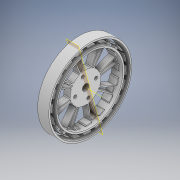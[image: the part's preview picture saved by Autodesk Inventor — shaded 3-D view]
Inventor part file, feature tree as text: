
AUTODESK INVENTOR PART (.ipt)
format: ipt  version: 2020 (Build 240168000, 168)  size: 643,072 bytes
history: native  units: mm
features: sketch x9, extrude x7, chamfer x2, pattern_circular x2, revolve x2, plane x1, fillet x1, other x1
ambient origin geometry x8: Origin, YZ Plane, XZ Plane, XY Plane, X Axis, Y Axis, Z Axis, Center Point
bodies: Solid1 (feature_tree)
feature tree (25):
  extrude  "Extrusion1"  Depth=7.0mm TaperAngle=0.0deg
  extrude  "Extrusion3"  Depth=80.0mm TaperAngle=360.0deg
  extrude  "Extrusion4"  Depth=7.0mm
  extrude  "Extrusion5"  Depth=13.6mm
  plane  "Work Plane2"
  sketch  "Sketch8"  dims[d25=4.0mm d26=2.0mm]
  extrude  "Extrusion7"  Depth=2.0mm
  extrude  "Extrusion8"  Depth=7.0mm TaperAngle=0.0deg
  chamfer  "Chamfer1"  Distance=7.0mm
  pattern_circular  "Circular Pattern1"  [2 undecoded]
  chamfer  "Chamfer2"  Distance=5.0mm
  fillet  "Fillet1"  Radius=0.5mm
  sketch  "Sketch10"  dims[d33=43.0mm]
  other  "Work Axis1"
  sketch  "Sketch11"  dims[d34=47.0mm]
  revolve  "Revolution2"  Angle=360.0deg
  revolve  "Revolution3"  Angle=45.0deg
  pattern_circular  "Circular Pattern2"  [2 undecoded]
  extrude  "Extrusion9"  Depth=6.0mm
  sketch  "Sketch1"  dims[d0=50.0mm d1=7.0mm d2=0.0mm]
  sketch  "Sketch3"  dims[d15=41.0mm d16=80.0mm d18=360.0deg]
  sketch  "Sketch4"  dims[d20=7.0mm d21=0.0mm d22=19.0mm]
  sketch  "Sketch5"  dims[d23=15.6mm d24=13.6mm]
  sketch  "Sketch9"  dims[d27=40.0mm d29=360.0deg d31=7.0mm d32=0.0mm]
  sketch  "Sketch12"  dims[d35=52.0mm d36=7.0mm d37=0.0mm d40=3.0mm d41=0.0mm d42=5.0mm d43=0.0mm d44=0.5mm d45=2.0mm d46=45.0deg d47=80.0mm d48=360.0deg d50=0.5mm d51=2.0mm d52=45.0deg d53=0.3mm d61=6.0mm d63=0.5mm d67=2.5mm d68=1.5mm d69=2.0mm d70=1.047198mm d71=2.094395mm d72=200.0mm d73=360.0deg d75=50.0mm d76=52.0mm d77=7.0mm d78=0.0mm d38=0.5mm d39=0.872665mm]
note: 4 required parameter values undecoded (feature->parameter linkage not recoverable at this tier; creation-order binding heuristic only, values carry confidence <= 0.55)
